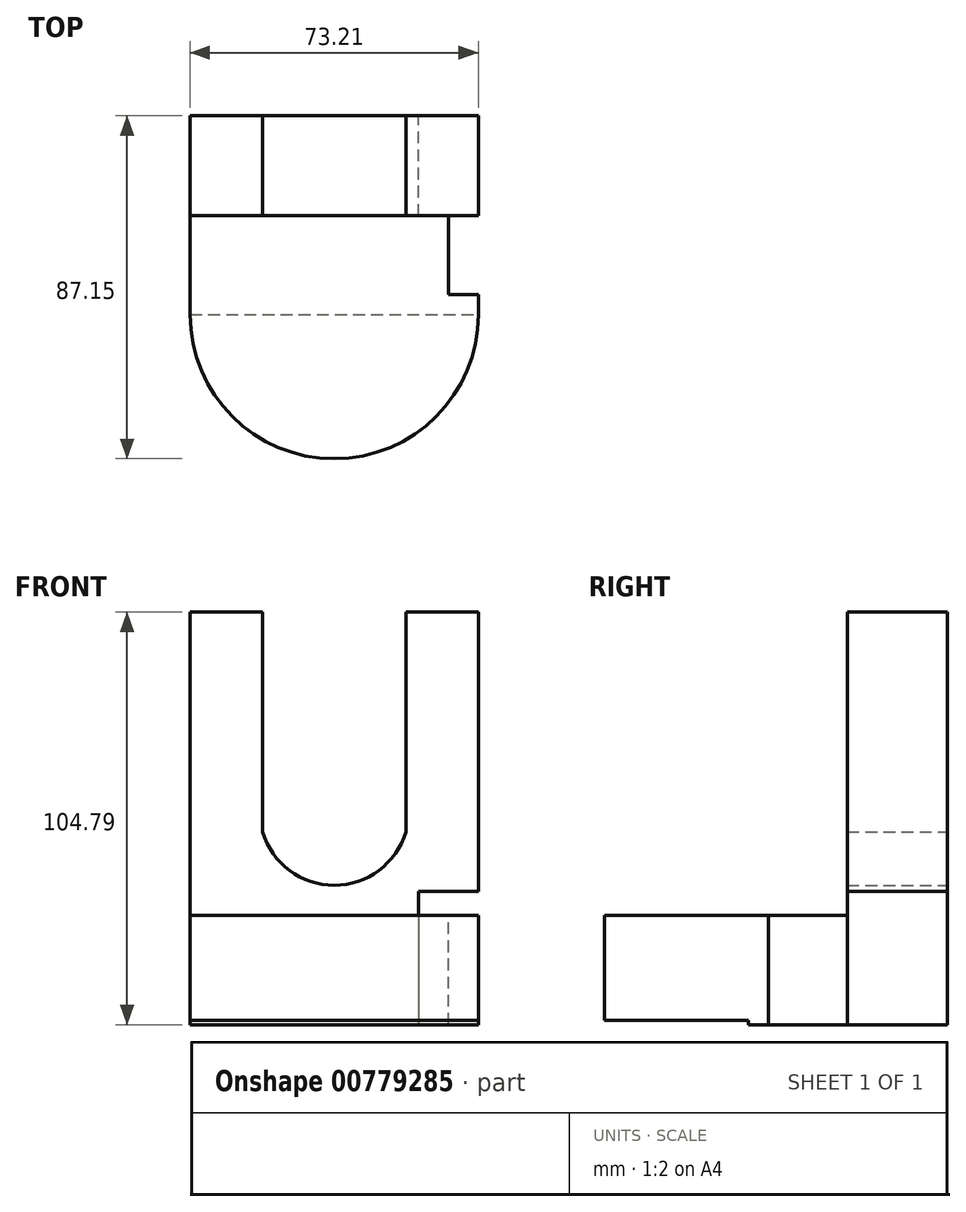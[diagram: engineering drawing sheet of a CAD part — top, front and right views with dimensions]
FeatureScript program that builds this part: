
annotation { "Feature Type Name" : "Feature", "Feature Type Description" : "" }
export const myFeature = defineFeature(function(context is Context, id is Id, definition is map)
    precondition{}
    {
        {
            var Q0;
            Q0=qCreatedBy(makeId("Front.planeOp"),FACE);
            var sketch = newSketch(context, id + "F0", { "sketchPlane" : qUnion([Q0])});
            skLineSegment(sketch, "E0.bottom", {"start": v(-73.21, 55.8) * mm, "end": v(-54.8, 55.8) * mm});
            skLineSegment(sketch, "E0.top", {"start": v(-73.21, -49) * mm, "end": v(0, -49) * mm});
            skLineSegment(sketch, "E0.left", {"start": v(-73.21, 55.8) * mm, "end": v(-73.21, -49) * mm});
            skLineSegment(sketch, "E0.right", {"start": v(0, 55.8) * mm, "end": v(0, -49) * mm});
            skLineSegment(sketch, "E1.left", {"start": v(-54.8, 55.8) * mm, "end": v(-54.8, 0) * mm});
            skLineSegment(sketch, "E1.right", {"start": v(-18.4, 55.8) * mm, "end": v(-18.4, 0) * mm});
            skLineSegment(sketch, "E2.trimOffspring", {"start": v(-18.4, 55.8) * mm, "end": v(0, 55.8) * mm});
            skArc(sketch, "E3", {"start": v(-54.8, 0) * mm, "mid": v(-36.6, -13.58) * mm, "end": v(-18.4, 0) * mm});
            skLineSegment(sketch, "E4.bottom", {"start": v(-73.21, -21.24) * mm, "end": v(0, -21.24) * mm});
            skLineSegment(sketch, "E4.left", {"start": v(-73.21, -21.24) * mm, "end": v(-73.21, -49) * mm});
            skLineSegment(sketch, "E4.right", {"start": v(0, -21.24) * mm, "end": v(0, -49) * mm});
            skSolve(sketch);
        }
        {
            var Q0;
            {var subQ4=sQuery(id+"F0.wireOp",EDGE,"E0.bottom");Q0=makeQuery(id+"F0.imprint","IMPRINT",FACE,{"disambiguationData":[TD([[makeQuery(id+"F0.imprint","IMPRINT",EDGE,{"derivedFrom":subQ4}),-1.0]])]});}
            extrude(context, id + "F1", {"entities" : qUnion([Q0]), "depth" : 25.4 * mm, "offsetDistance" : 25.4 * mm});
        }
        {
            var Q0;
            {var subQ0=sQuery(id+"F0.wireOp",EDGE,"E0.top");Q0=makeQuery(id+"F0.imprint","IMPRINT",FACE,{"disambiguationData":[TD([[makeQuery(id+"F0.imprint","IMPRINT",EDGE,{"derivedFrom":subQ0}),1.0]])]});}
            extrude(context, id + "F2", {"entities" : qUnion([Q0]), "operationType" : NewBodyOperationType.ADD, "depth" : 50.55 * mm, "offsetDistance" : 25.4 * mm});
        }
        {
            var Q0;
            Q0=makeQuery(id+"F2.opExtrude","SWEPT_FACE",FACE,{"disambiguationData":[OSD([sQuery(id+"F0.wireOp",EDGE,"E4.bottom")])]});
            var sketch = newSketch(context, id + "F3", { "sketchPlane" : qUnion([Q0])});
            skArc(sketch, "E5", {"start": v(-73.21, -50.55) * mm, "mid": v(-36.6, -87.15) * mm, "end": v(0, -50.55) * mm});
            skSolve(sketch);
        }
        {
            var Q0;
            Q0=makeQuery(id+"F3.imprint","IMPRINT",FACE,{"disambiguationData":[TD([[makeQuery(id+"F3.imprint","IMPRINT",EDGE,{"derivedFrom":sQuery(id+"F3.wireOp",EDGE,"E5")}),1.0]])]});
            extrude(context, id + "F4", {"entities" : qUnion([Q0]), "operationType" : NewBodyOperationType.ADD, "oppositeDirection" : true, "depth" : 26.67 * mm, "offsetDistance" : 25.4 * mm});
        }
        {
            var Q0;
            {var subQ0=sQuery(id+"F0.wireOp",EDGE,"E0.right");Q0=makeQuery(id+"F2.boolean.opBoolean","MERGE",FACE,{"derivedFrom":[makeQuery(id+"F1.opExtrude","SWEPT_FACE",FACE,{"disambiguationData":[OSD([subQ0])]}),makeQuery(id+"F2.opExtrude","SWEPT_FACE",FACE,{"disambiguationData":[OSD([subQ0])]})]});}
            var sketch = newSketch(context, id + "F5", { "sketchPlane" : qUnion([Q0])});
            skLineSegment(sketch, "E6.bottom", {"start": v(-25.4, -15.16) * mm, "end": v(0, -15.16) * mm});
            skLineSegment(sketch, "E6.top", {"start": v(-25.4, -49) * mm, "end": v(0, -49) * mm});
            skLineSegment(sketch, "E6.left", {"start": v(-25.4, -15.16) * mm, "end": v(-25.4, -49) * mm});
            skLineSegment(sketch, "E6.right", {"start": v(0, -15.16) * mm, "end": v(0, -49) * mm});
            skSolve(sketch);
        }
        {
            var Q0;
            Q0 = qSketchRegion(id + "F5", true);
            extrude(context, id + "F6", {"entities" : qUnion([Q0]), "operationType" : NewBodyOperationType.REMOVE, "oppositeDirection" : true, "depth" : 15.24 * mm, "offsetDistance" : 25.4 * mm});
        }
        {
            var Q0;
            {var subQ0=sQuery(id+"F0.wireOp",EDGE,"E4.bottom");Q0=makeQuery(id+"F4.boolean.opBoolean","MERGE",FACE,{"derivedFrom":[makeQuery(id+"F2.opExtrude","SWEPT_FACE",FACE,{"disambiguationData":[OSD([subQ0])]}),makeQuery(id+"F4.opExtrude","CAP_FACE",FACE,{"disambiguationData":[OSD([subQ0,sQuery(id+"F3.wireOp",EDGE,"E5")])],"isStart":true})]});}
            var sketch = newSketch(context, id + "F7", { "sketchPlane" : qUnion([Q0])});
            skLineSegment(sketch, "E7.bottom", {"start": v(-7.62, -25.4) * mm, "end": v(0, -25.4) * mm});
            skLineSegment(sketch, "E7.top", {"start": v(-7.62, -45.43) * mm, "end": v(0, -45.43) * mm});
            skLineSegment(sketch, "E7.left", {"start": v(-7.62, -25.4) * mm, "end": v(-7.62, -45.43) * mm});
            skLineSegment(sketch, "E7.right", {"start": v(0, -25.4) * mm, "end": v(0, -45.43) * mm});
            skSolve(sketch);
        }
        {
            var Q0;
            Q0 = qSketchRegion(id + "F7", true);
            extrude(context, id + "F8", {"entities" : qUnion([Q0]), "operationType" : NewBodyOperationType.REMOVE, "endBound" : BoundingType.THROUGH_ALL, "oppositeDirection" : true, "depth" : 25.4 * mm, "offsetDistance" : 25.4 * mm});
        }
    });
